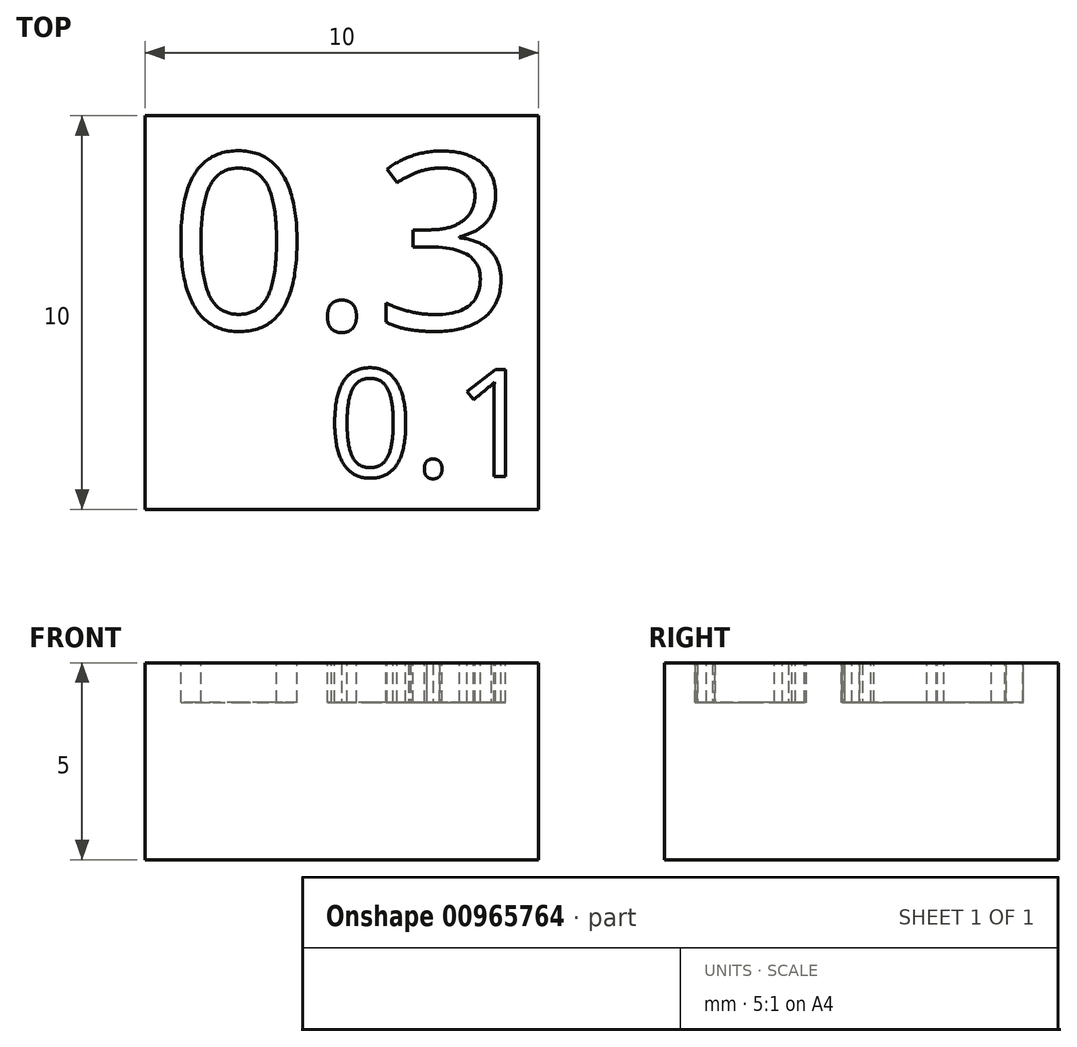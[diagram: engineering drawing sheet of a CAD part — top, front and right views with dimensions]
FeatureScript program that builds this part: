
annotation { "Feature Type Name" : "Feature", "Feature Type Description" : "" }
export const myFeature = defineFeature(function(context is Context, id is Id, definition is map)
    precondition{}
    {
        {
            var Q0;
            Q0=qCreatedBy(makeId("Top.planeOp"),FACE);
            var sketch = newSketch(context, id + "F0", { "sketchPlane" : qUnion([Q0])});
            skLineSegment(sketch, "E0.bottom", {"start": v(5, -5) * mm, "end": v(-5, -5) * mm});
            skLineSegment(sketch, "E0.top", {"start": v(5, 5) * mm, "end": v(-5, 5) * mm});
            skLineSegment(sketch, "E0.left", {"start": v(5, -5) * mm, "end": v(5, 5) * mm});
            skLineSegment(sketch, "E0.right", {"start": v(-5, -5) * mm, "end": v(-5, 5) * mm});
            skSolve(sketch);
        }
        {
            var Q0;
            Q0=makeQuery(id+"F0.imprint","IMPRINT",FACE,{"disambiguationData":[TD([[makeQuery(id+"F0.imprint","IMPRINT",EDGE,{"derivedFrom":sQuery(id+"F0.wireOp",EDGE,"E0.bottom")}),-1.0]])]});
            var Q1;
            Q1=makeQuery(id+"F0.imprint","IMPRINT",FACE,{"disambiguationData":[TD([[makeQuery(id+"F0.imprint","IMPRINT",EDGE,{"derivedFrom":sQuery(id+"F0.wireOp",EDGE,"59c123fb-ddb5-4ba9-8e25-1d5593d6517a.sketch_text.stroke-8")}),1.0]])]});
            var Q2;
            Q2=makeQuery(id+"F0.imprint","IMPRINT",FACE,{"disambiguationData":[TD([[makeQuery(id+"F0.imprint","IMPRINT",EDGE,{"derivedFrom":sQuery(id+"F0.wireOp",EDGE,"ef4e36e8-8281-47e3-beb4-d553aacd2ff7.sketch_text.stroke-8")}),1.0]])]});
            extrude(context, id + "F1", {"entities" : qUnion([Q0, Q1, Q2]), "depth" : 5 * mm, "offsetDistance" : 25 * mm});
        }
        {
            var Q0;
            Q0=makeQuery(id+"F1.opExtrude","CAP_FACE",FACE,{"disambiguationData":[OSD([sQuery(id+"F0.wireOp",EDGE,"E0.bottom"),sQuery(id+"F0.wireOp",EDGE,"E0.top"),sQuery(id+"F0.wireOp",EDGE,"E0.left"),sQuery(id+"F0.wireOp",EDGE,"E0.right")])],"isStart":false});
            var sketch = newSketch(context, id + "F2", { "sketchPlane" : qUnion([Q0])});
            skText(sketch, "E1", { "text": "0.3", "fontName": "OpenSans-Regular.ttf"});
            skText(sketch, "E2", { "text": "0.1", "fontName": "OpenSans-Regular.ttf"});
            const initialGuessF2  = {"E1": [-0.0044, -0.00042, 1, 0, 0.0045], "E2": [-0.00037, -0.00417, 1, 0, 0.00275]};
            skSetInitialGuess(sketch, initialGuessF2);
            skSolve(sketch);
        }
        {
            var Q0;
            Q0=makeQuery(id+"F2.imprint","IMPRINT",FACE,{"disambiguationData":[TD([[makeQuery(id+"F2.imprint","IMPRINT",EDGE,{"derivedFrom":sQuery(id+"F2.wireOp",EDGE,"E1.sketch_text.stroke-0")}),-1.0]])]});
            var Q1;
            Q1=makeQuery(id+"F2.imprint","IMPRINT",FACE,{"disambiguationData":[TD([[makeQuery(id+"F2.imprint","IMPRINT",EDGE,{"derivedFrom":sQuery(id+"F2.wireOp",EDGE,"E1.sketch_text.stroke-16")}),-1.0]])]});
            var Q2;
            Q2=makeQuery(id+"F2.imprint","IMPRINT",FACE,{"disambiguationData":[TD([[makeQuery(id+"F2.imprint","IMPRINT",EDGE,{"derivedFrom":sQuery(id+"F2.wireOp",EDGE,"E1.sketch_text.stroke-24")}),-1.0]])]});
            var Q3;
            Q3=makeQuery(id+"F2.imprint","IMPRINT",FACE,{"disambiguationData":[TD([[makeQuery(id+"F2.imprint","IMPRINT",EDGE,{"derivedFrom":sQuery(id+"F2.wireOp",EDGE,"E2.sketch_text.stroke-0")}),-1.0]])]});
            var Q4;
            Q4=makeQuery(id+"F2.imprint","IMPRINT",FACE,{"disambiguationData":[TD([[makeQuery(id+"F2.imprint","IMPRINT",EDGE,{"derivedFrom":sQuery(id+"F2.wireOp",EDGE,"E2.sketch_text.stroke-16")}),-1.0]])]});
            var Q5;
            Q5=makeQuery(id+"F2.imprint","IMPRINT",FACE,{"disambiguationData":[TD([[makeQuery(id+"F2.imprint","IMPRINT",EDGE,{"derivedFrom":sQuery(id+"F2.wireOp",EDGE,"E2.sketch_text.stroke-24")}),-1.0]])]});
            extrude(context, id + "F3", {"entities" : qUnion([Q0, Q1, Q2, Q3, Q4, Q5]), "operationType" : NewBodyOperationType.REMOVE, "oppositeDirection" : true, "depth" : 1 * mm, "offsetDistance" : 25 * mm});
        }
    });
